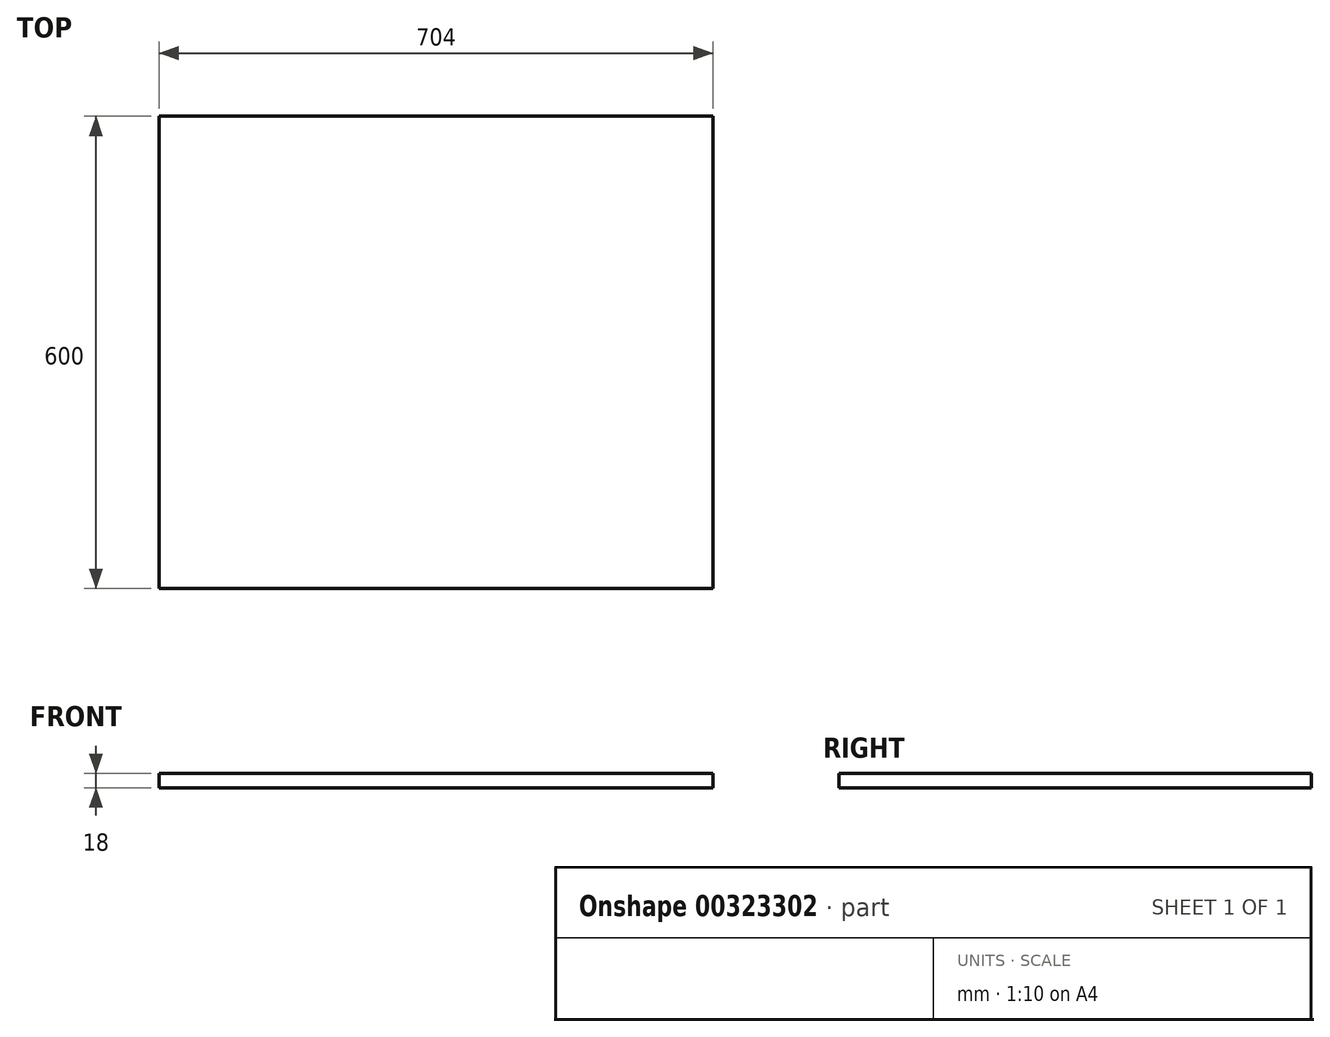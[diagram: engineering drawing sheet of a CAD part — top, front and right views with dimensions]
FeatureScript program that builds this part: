
annotation { "Feature Type Name" : "Feature", "Feature Type Description" : "" }
export const myFeature = defineFeature(function(context is Context, id is Id, definition is map)
    precondition{}
    {
        {
            var Q0;
            Q0=qCreatedBy(makeId("Top.planeOp"),FACE);
            var sketch = newSketch(context, id + "F0", { "sketchPlane" : qUnion([Q0])});
            skLineSegment(sketch, "E0.bottom", {"start": v(0, 0) * mm, "end": v(704, 0) * mm});
            skLineSegment(sketch, "E0.top", {"start": v(0, 600) * mm, "end": v(704, 600) * mm});
            skLineSegment(sketch, "E0.left", {"start": v(0, 0) * mm, "end": v(0, 600) * mm});
            skLineSegment(sketch, "E0.right", {"start": v(704, 0) * mm, "end": v(704, 600) * mm});
            skSolve(sketch);
        }
        {
            var Q0;
            Q0 = qSketchRegion(id + "F0", true);
            extrude(context, id + "F1", {"entities" : qUnion([Q0]), "depth" : 18 * mm, "offsetDistance" : 25 * mm});
        }
    });
